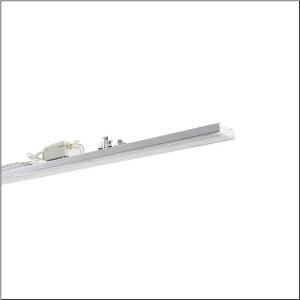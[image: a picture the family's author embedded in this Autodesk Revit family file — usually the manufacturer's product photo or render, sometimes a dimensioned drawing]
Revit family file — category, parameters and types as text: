
# Revit family: licross_11_recessed_mo_51te107n485g
name_source: partatom
category: Lighting Fixtures
units: mm (PartAtom-declared; Revit-internal decimal feet)

## family parameters
Cut with Voids When Loaded = No
Host = Face
Light Source = No
Part Type = Normal
Room Calculation Point = No
Round Connector Dimension = Use Diameter
Shared = No

## types (1)
- Licross 11 Recessed MO (1 x LED, 8700 lm, 48.5 W, 4000K)
    Apparent Load = 49 VA
    CIE Flux Codes = 50 81 96 100 100
    Color Rendering = 80
    Color Temperature = 4000K
    Default Elevation = 1800 mm
    Description = Licross 11 Recessed MO, luminaire insert, of sheet steel, galvanised, coil coated, white, length: 1.500mm, width: 66mm, height: 67mm, LED rated luminous flux: 8.710lm, light colour: 840, SDCM (Standard Deviation of Colour Matching)MacAdam ≤ 2 SDCM (initial), control gear: ON/OFF, with plug, 3-pole, with phase selection, mains connection: 220..240V, AC, 50/60Hz, rated input power: 49W, internal wiring halogen-free, primary optical cover: cover, of PMMA, light emission: direct distribution, primary light characteristic: symmetric, protection rating (complete): IP54, insulation class (complete): insulation class I (protective earthing), certification: CE, ENEC, VDE, UKCA, protection symbol: D if used in an environment with non-conductive dust loads with corresponding accessories, impact resistance: IK06, permissible ambient temperature for indoor applications: -35..+35°C, corresponds to IFS (International Featured Standards) requirements for safety and quality in the food industry, reducing of maximum allowable ambient temperature of 5°C with ceiling mounting, The light source and the operating device comply with the requirements of the Ecodesign Regulation (EU) 2019/2020 and are replaceable in accordance with this regulation, packaging unit: 1 piece
    Height = 58 mm
    Lamp = 1 x LED
    Lamp Light Flux = 8700 lm
    Lamp Power = 48.5 W
    Lamp count = 1
    Length = 1500 mm
    Luminous efficacy = 179 lm/W
    Manufacturer = Siteco
    ModVariant = No
    Model = 51TE107N485G
    Mounting Place = Ceiling
    Mounting Type = Pendant
    Number of Poles = 1
    OnlyDefault = Yes
    Power Factor = 1
    Product Name = Licross 11 Recessed MO
    Product group = luminaire insert | ceiling pendant
    ProductGroupID = 901
    Protection Class = Protection class I
    Protection Degree = IP 54
    RLX_Detail_Level = 1
    RLX_Emergency_Light_Flux = 0 lm
    RLX_Emergency_Type = 0
    RLX_Emergency_Type_DB = No
    RlxData = <blob elided: 20973 chars, md5=feb7991c>
    Socket = socket
    Standby Power = 0 W
    System Light Flux = 8700 lm
    System Power = 49 W
    Type Comments = Product without accessories
    Type Image = l_1296930.jpg
    URL = http://relux.com
    VarID = ---
    Voltage = 0 V
    Weight = 0.00 kg
    Width = 66 mm

## geometry (parser evidence)
native form markers: Blend x4, Sweep x11
no freeform markers — native parametric forms only
